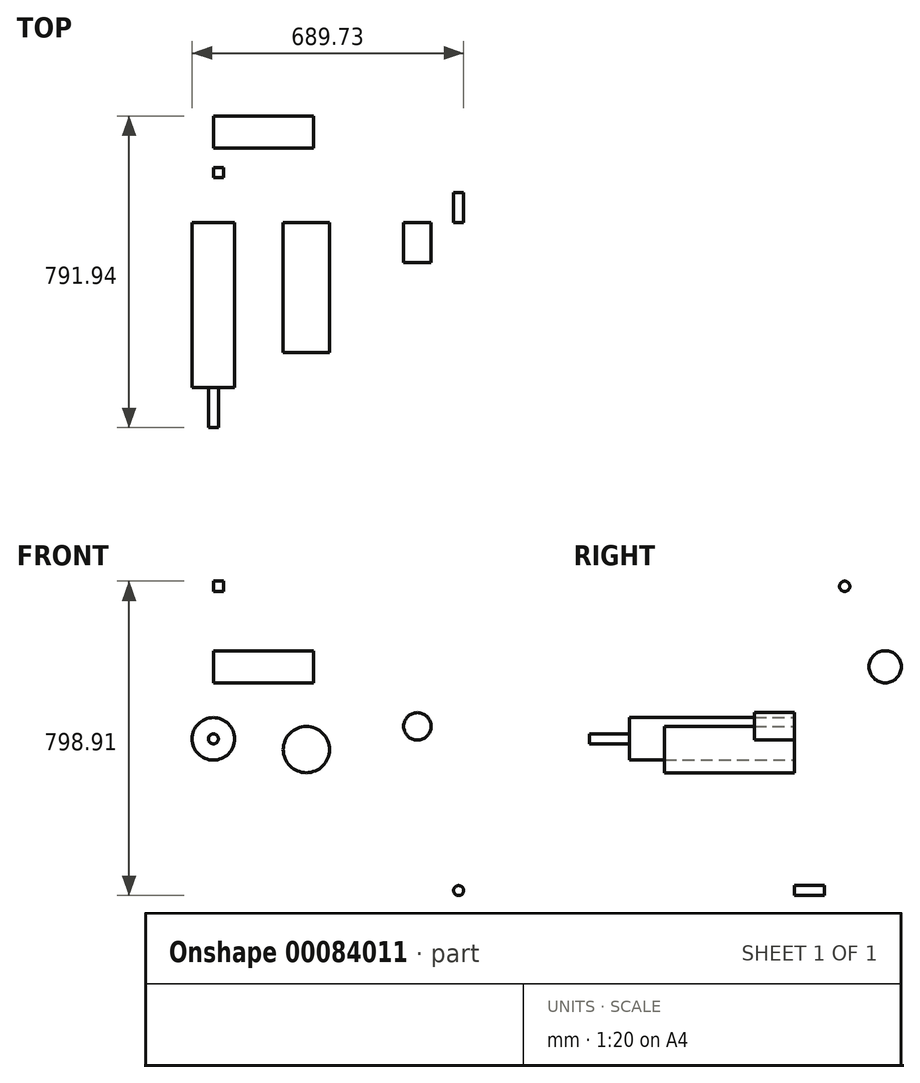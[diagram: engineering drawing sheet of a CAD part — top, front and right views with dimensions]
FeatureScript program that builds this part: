
annotation { "Feature Type Name" : "Feature", "Feature Type Description" : "" }
export const myFeature = defineFeature(function(context is Context, id is Id, definition is map)
    precondition{}
    {
        {
            var Q0;
            Q0=qCreatedBy(makeId("Front.planeOp"),FACE);
            var sketch = newSketch(context, id + "F0", { "sketchPlane" : qUnion([Q0])});
            skCircle(sketch, "E0", {"center": v(0, 0) * mm, "radius": 53.98 * mm});
            skSolve(sketch);
        }
        {
            var Q0;
            Q0=makeQuery(id+"F0.imprint","IMPRINT",FACE,{"disambiguationData":[TD([[makeQuery(id+"F0.imprint","IMPRINT",EDGE,{"derivedFrom":sQuery(id+"F0.wireOp",EDGE,"E0")}),1.0]])]});
            extrude(context, id + "F1", {"entities" : qUnion([Q0]), "depth" : 419.1 * mm});
        }
        {
            var Q0;
            Q0=makeQuery(id+"F1.opExtrude","CAP_FACE",FACE,{"disambiguationData":[OSD([sQuery(id+"F0.wireOp",EDGE,"E0")])],"isStart":false});
            var sketch = newSketch(context, id + "F2", { "sketchPlane" : qUnion([Q0])});
            skCircle(sketch, "E1", {"center": v(0, 0) * mm, "radius": 12.7 * mm});
            skSolve(sketch);
        }
        {
            var Q0;
            Q0=makeQuery(id+"F2.imprint","IMPRINT",FACE,{"disambiguationData":[TD([[makeQuery(id+"F2.imprint","IMPRINT",EDGE,{"derivedFrom":sQuery(id+"F2.wireOp",EDGE,"E1")}),1.0]])]});
            extrude(context, id + "F3", {"entities" : qUnion([Q0]), "operationType" : NewBodyOperationType.ADD, "depth" : 101.6 * mm});
        }
        {
            var Q0;
            Q0=qCreatedBy(makeId("Right.planeOp"),FACE);
            var sketch = newSketch(context, id + "F4", { "sketchPlane" : qUnion([Q0])});
            skCircle(sketch, "E2", {"center": v(230.33, 183.1) * mm, "radius": 40.91 * mm});
            skSolve(sketch);
        }
        {
            var Q0;
            Q0 = qSketchRegion(id + "F4", true);
            extrude(context, id + "F5", {"entities" : qUnion([Q0]), "depth" : 254 * mm});
        }
        {
            var Q0;
            Q0=qCreatedBy(makeId("Right.planeOp"),FACE);
            var sketch = newSketch(context, id + "F6", { "sketchPlane" : qUnion([Q0])});
            skCircle(sketch, "E3", {"center": v(127.35, 387.64) * mm, "radius": 13.12 * mm});
            skSolve(sketch);
        }
        {
            var Q0;
            Q0 = qSketchRegion(id + "F6", true);
            extrude(context, id + "F7", {"entities" : qUnion([Q0]), "depth" : 25.4 * mm});
        }
        {
            var Q0;
            Q0 = qSketchRegion(id + "F0", true);
            var Q1;
            Q1 = qSketchRegion(id + "F13", true);
            extrude(context, id + "F8", {"entities" : qUnion([Q0, Q1]), "operationType" : NewBodyOperationType.ADD, "depth" : 25.4 * mm});
        }
        {
            var Q0;
            Q0=makeQuery(id+"F1.opExtrude","CAP_FACE",FACE,{"disambiguationData":[OSD([sQuery(id+"F0.wireOp",EDGE,"E0")])],"isStart":true});
            var sketch = newSketch(context, id + "F9", { "sketchPlane" : qUnion([Q0])});
            skCircle(sketch, "E4", {"center": v(-623.05, -385.45) * mm, "radius": 12.7 * mm});
            skSolve(sketch);
        }
        {
            var Q0;
            Q0 = qSketchRegion(id + "F9", true);
            extrude(context, id + "F10", {"entities" : qUnion([Q0]), "depth" : 76.2 * mm});
        }
        {
            var Q0;
            Q0=qCreatedBy(makeId("Front.planeOp"),FACE);
            var sketch = newSketch(context, id + "F11", { "sketchPlane" : qUnion([Q0])});
            skCircle(sketch, "E5", {"center": v(518.3, 31.8) * mm, "radius": 34.8 * mm});
            skSolve(sketch);
        }
        {
            var Q0;
            Q0=makeQuery(id+"F11.imprint","IMPRINT",FACE,{"disambiguationData":[TD([[makeQuery(id+"F11.imprint","IMPRINT",EDGE,{"derivedFrom":sQuery(id+"F11.wireOp",EDGE,"E5")}),1.0]])]});
            extrude(context, id + "F12", {"entities" : qUnion([Q0]), "depth" : 101.6 * mm});
        }
        {
            var Q0;
            Q0=qCreatedBy(makeId("Front.planeOp"),FACE);
            var sketch = newSketch(context, id + "F13", { "sketchPlane" : qUnion([Q0])});
            skCircle(sketch, "E6", {"center": v(236.36, -27.17) * mm, "radius": 58.74 * mm});
            skSolve(sketch);
        }
        {
            var Q0;
            Q0=sQuery(id+"F13.wireOp",EDGE,"E6");
            extrude(context, id + "F14", {"bodyType" : ToolBodyType.SURFACE, "surfaceEntities" : qUnion([Q0]), "depth" : 330.2 * mm});
        }
        {
            var Q0;
            Q0=makeQuery(id+"F13.imprint","IMPRINT",FACE,{"disambiguationData":[TD([[makeQuery(id+"F13.imprint","IMPRINT",EDGE,{"derivedFrom":sQuery(id+"F13.wireOp",EDGE,"E6")}),1.0]])]});
            extrude(context, id + "F15", {"entities" : qUnion([Q0]), "depth" : 330.2 * mm});
        }
        {
            var Q0;
            Q0=makeQuery(id+"F14.opExtrude","SWEPT_BODY",BODY,{"disambiguationData":[OSD([sQuery(id+"F13.wireOp",EDGE,"E6")])]});
            deleteBodies(context, id + "F16", {"entities" : qUnion([Q0])});
        }
    });
